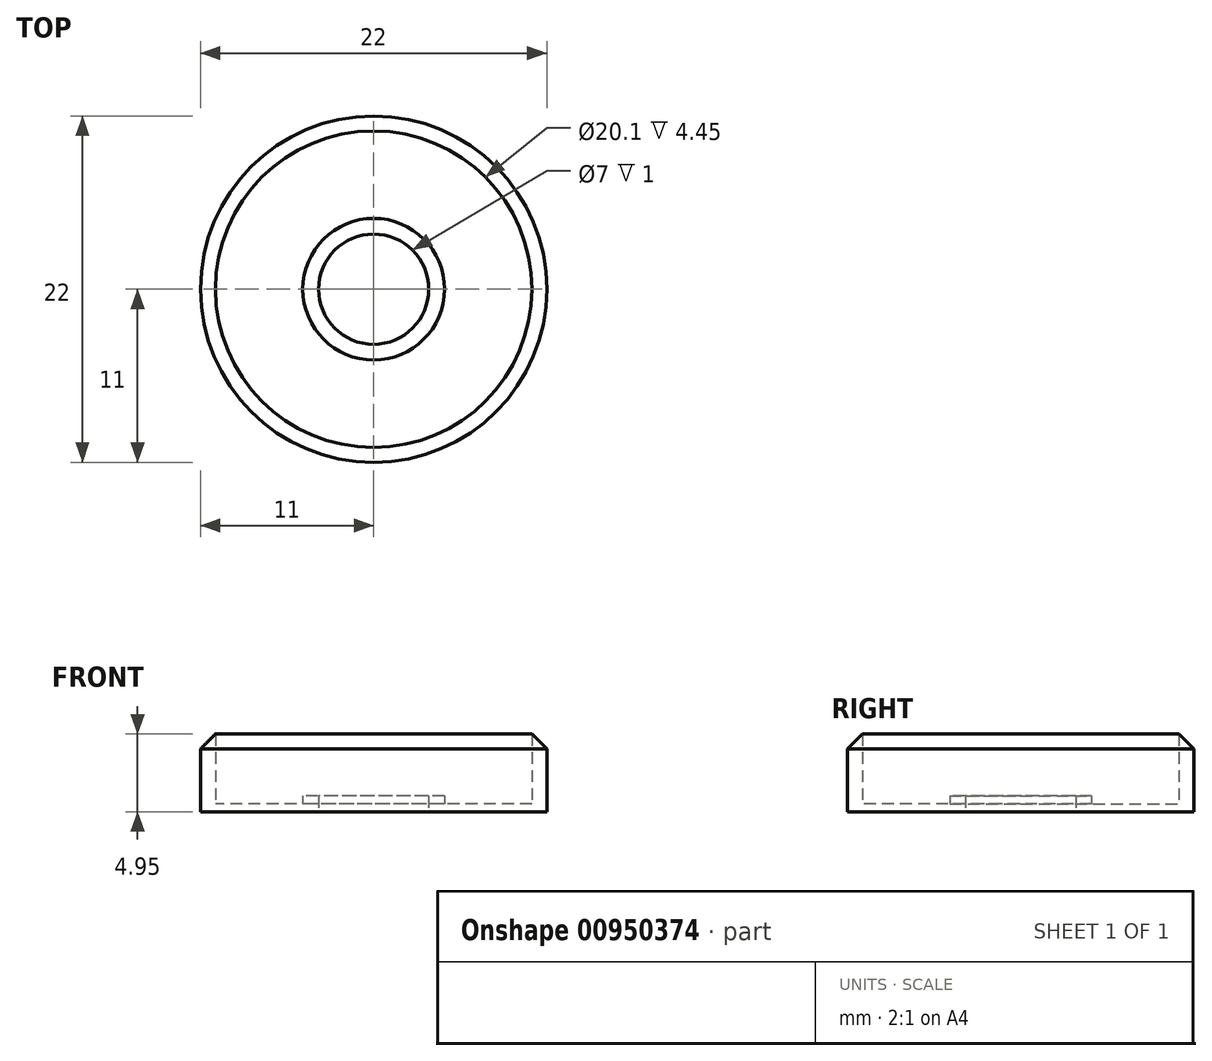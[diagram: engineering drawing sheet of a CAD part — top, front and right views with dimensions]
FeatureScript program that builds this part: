
annotation { "Feature Type Name" : "Feature", "Feature Type Description" : "" }
export const myFeature = defineFeature(function(context is Context, id is Id, definition is map)
    precondition{}
    {
        {
            var Q0;
            Q0=qCreatedBy(makeId("Top.planeOp"),FACE);
            var sketch = newSketch(context, id + "F0", { "sketchPlane" : qUnion([Q0])});
            skCircle(sketch, "E0", {"center": v(0, 0) * mm, "radius": 10.05 * mm});
            skCircle(sketch, "E1", {"center": v(0, 0) * mm, "radius": 11 * mm});
            skCircle(sketch, "E2", {"center": v(0, 0) * mm, "radius": 10.5 * mm});
            skCircle(sketch, "E3", {"center": v(0, 0) * mm, "radius": 3.5 * mm});
            skCircle(sketch, "E4", {"center": v(0, 0) * mm, "radius": 4.5 * mm});
            skSolve(sketch);
        }
        {
            var Q0;
            Q0=qSketchRegion(id+"F0",true);
            var Q1;
            Q1=makeQuery(id+"F0.imprint","IMPRINT",FACE,{"disambiguationData":[TD([[makeQuery(id+"F0.imprint","IMPRINT",EDGE,{"derivedFrom":sQuery(id+"F0.wireOp",EDGE,"E0")}),-1.0]])]});
            extrude(context, id + "F1", {"entities" : qUnion([Q0, Q1]), "depth" : 5 * mm, "offsetDistance" : 25 * mm});
        }
        {
            var Q0;
            Q0=qCreatedBy(makeId("Front.planeOp"),FACE);
            var sketch = newSketch(context, id + "F2", { "sketchPlane" : qUnion([Q0])});
            skLineSegment(sketch, "E5", {"start": v(0, 0) * mm, "end": v(0, 5) * mm});
            skLineSegment(sketch, "E6", {"start": v(0, 0) * mm, "end": v(0, 2.5) * mm});
            skSolve(sketch);
        }
        {
            var Q0;
            Q0=sQuery(id+"F2.wireOp",VERTEX,"E6.end");
            var Q1;
            Q1=qCreatedBy(makeId("Top.planeOp"),FACE);
            cPlane(context, id + "F3", {"entities" : qUnion([Q0, Q1]), "cplaneType" : CPlaneType.PLANE_POINT, "offset" : 25 * mm, "width" : 150 * mm, "height" : 150 * mm});
        }
        {
            var Q0;
            Q0=qCreatedBy(id+"F3.planeOp",FACE);
            var sketch = newSketch(context, id + "F4", { "sketchPlane" : qUnion([Q0])});
            skCircle(sketch, "E7", {"center": v(0, 0) * mm, "radius": 10.5 * mm});
            skCircle(sketch, "E8", {"center": v(0, 0) * mm, "radius": 11 * mm});
            skSolve(sketch);
        }
        {
            var Q0;
            Q0=makeQuery(id+"F1.opExtrude","CAP_EDGE",EDGE,{"disambiguationData":[OSD([sQuery(id+"F0.wireOp",EDGE,"E1")])],"isStart":false});
            chamfer(context, id + "F5", {"entities" : qUnion([Q0]), "width" : 1 * mm, "tangentPropagation" : true});
        }
        {
            var Q0;
            Q0=makeQuery(id+"F0.imprint","IMPRINT",FACE,{"disambiguationData":[TD([[makeQuery(id+"F0.imprint","IMPRINT",EDGE,{"derivedFrom":sQuery(id+"F0.wireOp",EDGE,"E0")}),1.0]])]});
            extrude(context, id + "F6", {"entities" : qUnion([Q0]), "operationType" : NewBodyOperationType.ADD, "depth" : .5 * mm, "offsetDistance" : 25 * mm});
        }
        {
            var Q0;
            Q0=makeQuery(id+"F0.imprint","IMPRINT",FACE,{"disambiguationData":[TD([[makeQuery(id+"F0.imprint","IMPRINT",EDGE,{"derivedFrom":sQuery(id+"F0.wireOp",EDGE,"E3")}),-1.0]])]});
            extrude(context, id + "F7", {"entities" : qUnion([Q0]), "operationType" : NewBodyOperationType.ADD, "depth" : 1 * mm, "offsetDistance" : 25 * mm});
        }
    });
